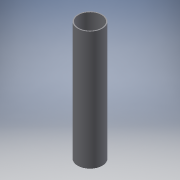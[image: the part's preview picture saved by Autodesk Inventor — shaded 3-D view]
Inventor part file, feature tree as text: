
AUTODESK INVENTOR PART (.ipt)
format: ipt  version: 2018 (Build 220112000, 112)  size: 95,232 bytes
history: native  units: in
note: dims shown in document units (in); Inventor stores cm internally (conversion verified against a paired STEP export)
features: extrude x1, sketch x1
ambient origin geometry x8: Origin, YZ Plane, XZ Plane, XY Plane, X Axis, Y Axis, Z Axis, Center Point
bodies: Solid1 (feature_tree)
feature tree (2):
  extrude  "Extrusion1"  Depth=6.0in
  sketch  "Sketch1"  dims[d0=1.25in d1=1.15in d2=6.0in d3=0.0in]
